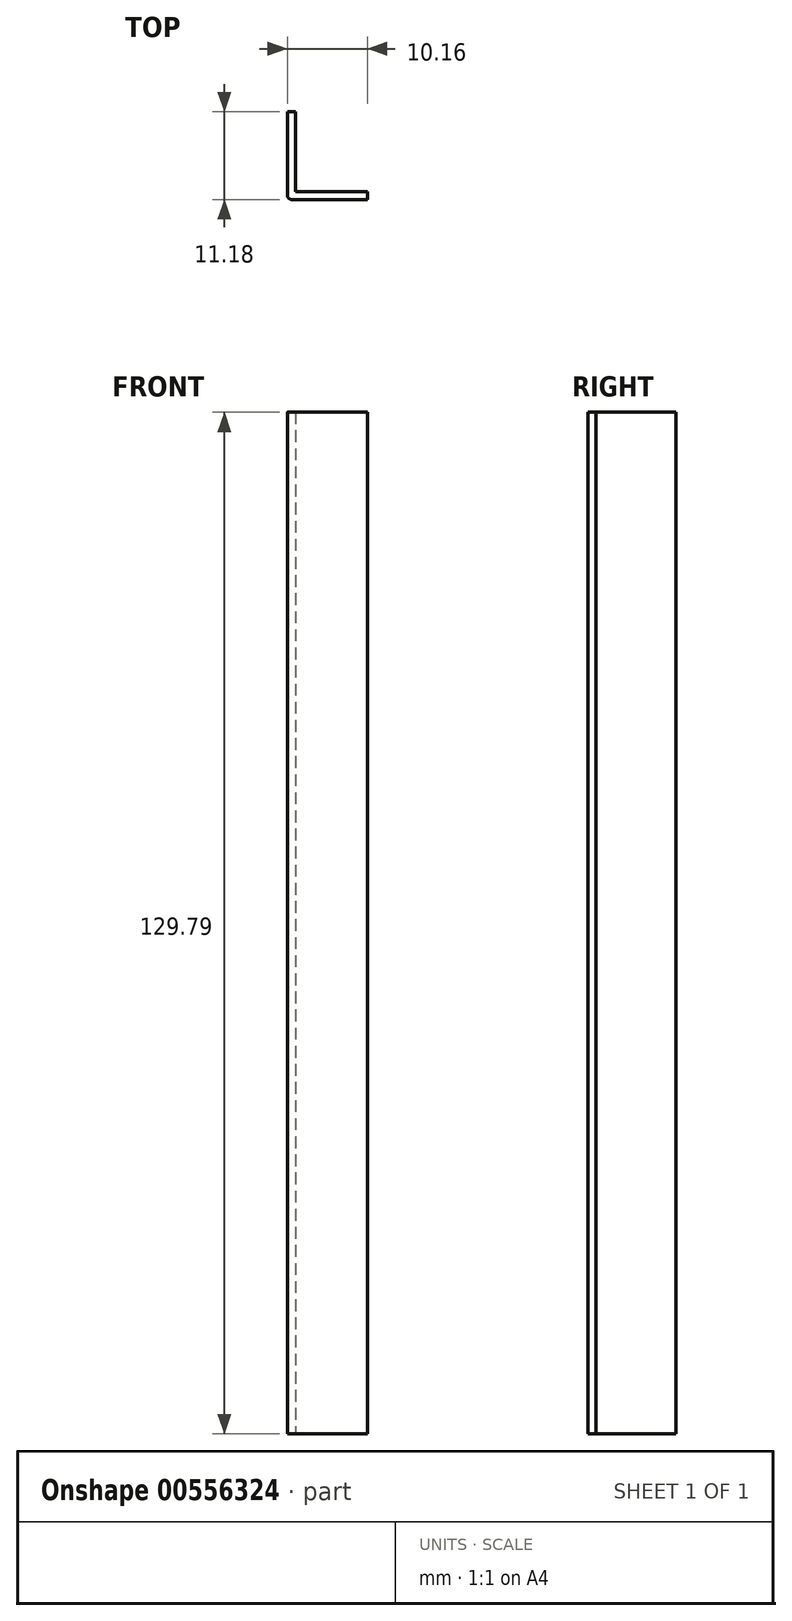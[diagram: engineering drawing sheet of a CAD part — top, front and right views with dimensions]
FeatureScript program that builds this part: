
annotation { "Feature Type Name" : "Feature", "Feature Type Description" : "" }
export const myFeature = defineFeature(function(context is Context, id is Id, definition is map)
    precondition{}
    {
        {
            var Q0;
            Q0=qCreatedBy(makeId("Top.planeOp"),FACE);
            var sketch = newSketch(context, id + "F0", { "sketchPlane" : qUnion([Q0])});
            skLineSegment(sketch, "E0.bottom", {"start": v(0, 0) * mm, "end": v(-10.16, 0) * mm});
            skLineSegment(sketch, "E0.top", {"start": v(0, -1.02) * mm, "end": v(-10.16, -1.02) * mm});
            skLineSegment(sketch, "E0.left", {"start": v(0, 0) * mm, "end": v(0, -1.02) * mm});
            skLineSegment(sketch, "E0.right", {"start": v(-10.16, 0) * mm, "end": v(-10.16, -1.02) * mm});
            skLineSegment(sketch, "E1.bottom", {"start": v(-10.16, 0) * mm, "end": v(-9.14, 0) * mm});
            skLineSegment(sketch, "E1.top", {"start": v(-10.16, 10.16) * mm, "end": v(-9.14, 10.16) * mm});
            skLineSegment(sketch, "E1.left", {"start": v(-10.16, 0) * mm, "end": v(-10.16, 10.16) * mm});
            skLineSegment(sketch, "E1.right", {"start": v(-9.14, 0) * mm, "end": v(-9.14, 10.16) * mm});
            skSolve(sketch);
        }
        {
            var Q0;
            Q0 = qSketchRegion(id + "F0", true);
            extrude(context, id + "F1", {"entities" : qUnion([Q0]), "depth" : 129.8 * mm, "offsetDistance" : 25.4 * mm});
        }
        {
            var Q0;
            Q0=makeQuery(id+"F1.opExtrude","SWEPT_EDGE",EDGE,{"disambiguationData":[OSD([sQuery(id+"F0.wireOp",EDGE,"E0.top"),sQuery(id+"F0.wireOp",EDGE,"E0.right")])]});
            fillet(context, id + "F2", {"entities" : qUnion([Q0]), "radius" : 0.64 * mm, "tangentPropagation" : true, "allowEdgeOverflow" : false});
        }
    });
